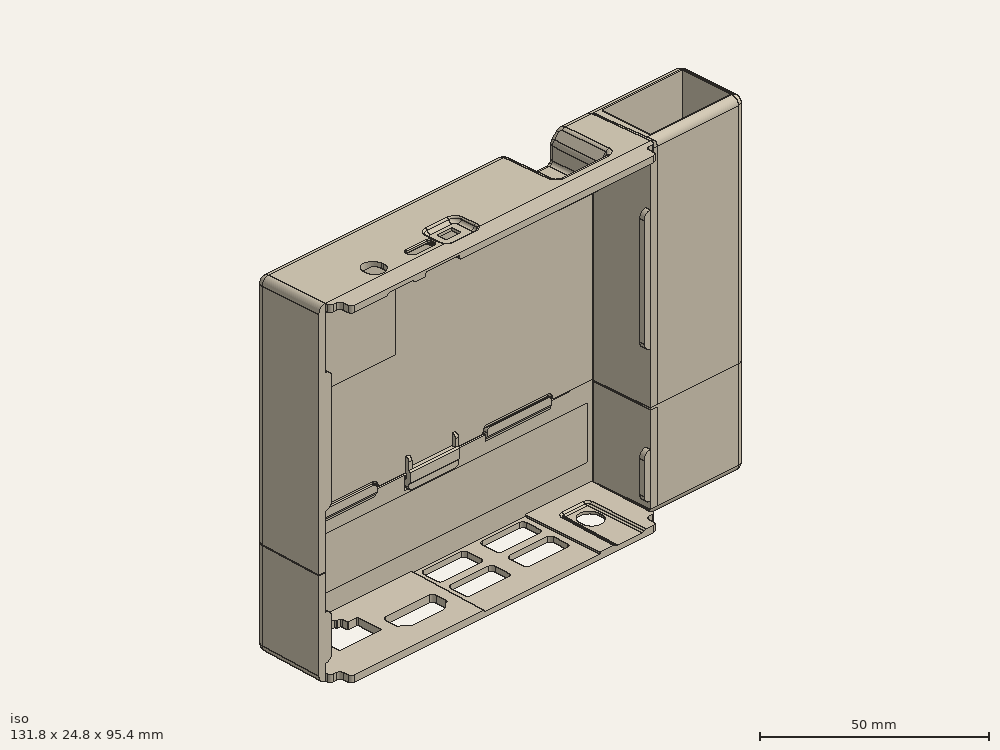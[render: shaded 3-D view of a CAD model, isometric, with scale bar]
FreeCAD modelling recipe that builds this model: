
FCSTD DOCUMENT  (FreeCAD 0.20R29177 +233 (Git))
Label: N2Case_10_11_2022
License: All rights reserved
LicenseURL: http://en.wikipedia.org/wiki/All_rights_reserved
objects: Part::Box×22, Part::Cylinder×11, Part::MultiFuse×9, Part::Cut×9, Part::Sphere×4, Part::Feature×2, Sketcher::SketchObject×2, PartDesign::Pad×2, PartDesign::Body×2
note: 65 computed .brp shape members not serialized (recipe doc carries the construction recipe); baked Part::Feature solids carry a one-line shape summary decoded from their .brp

FEATURE [Part::Feature] Solid  label="N2_BOTTOM_COVER"
  shape: bbox 104.6 x 25.21 x 71.78 mm, 343 faces (baked)
FEATURE [Part::Feature] Solid001  label="N2_TOP_COVER"
  shape: bbox 104.6 x 24.81 x 29.22 mm, 349 faces (baked)
FEATURE [Part::Box] Box  label="Cube"
  AttacherType = Attacher::AttachEngine3D
  Height = 15
  Length = 62.5
  Placement = pos=(-49,18,44) rot=(0,-1,0;4.71239rad)
  Width = 2
FEATURE [Part::MultiFuse] Fusion  label="BottomCover"
  Shapes = -> [Solid,Box]
FEATURE [Part::Box] Box001  label="Cube001"
  AttacherType = Attacher::AttachEngine3D
  Height = 15
  Length = 97.5
  Placement = pos=(48.5,20,-3.5) rot=(0,1,0;3.14159rad)
  Width = 2
FEATURE [Part::Cut] Cut
  Base = -> Fusion
  Tool = -> Box001
FEATURE [Part::Box] Box002  label="usbEthernet"
  AttacherType = Attacher::AttachEngine3D
  Height = 25
  Length = 72
  Placement = pos=(52.5,2.6,47.4) rot=(0,1,0;1.5708rad)
  Width = 15
FEATURE [Part::Box] Box003  label="usbEthernetCover"
  AttacherType = Attacher::AttachEngine3D
  Height = 27.5
  Length = 72
  Placement = pos=(50.5,2.2,47.4) rot=(0,1,0;1.5708rad)
  Width = 15.85
FEATURE [Part::Box] Box004  label="usbEthernetCover001"
  AttacherType = Attacher::AttachEngine3D
  Height = 27.52
  Length = 65.19
  Placement = pos=(49.98,17.6,45.39) rot=(0,1,0;1.5708rad)
  Width = 2.4
FEATURE [Part::Box] Box005  label="usbEthernetCover002"
  AttacherType = Attacher::AttachEngine3D
  Height = 2
  Length = 65.19
  Placement = pos=(77.5,2.2,45.39) rot=(0,1,0;1.5708rad)
  Width = 15.8
FEATURE [Part::Cylinder] Cylinder
  Angle = 90
  AttacherType = Attacher::AttachEngine3D
  FirstAngle = 0
  Height = 65.2
  Placement = pos=(77.5,2.2,-19.8) rot=(0,0,1;4.71239rad)
  Radius = 2
  SecondAngle = 0
FEATURE [Part::Cylinder] Cylinder001
  Angle = 90
  AttacherType = Attacher::AttachEngine3D
  FirstAngle = 0
  Height = 27.5
  Placement = pos=(77.5,18,45.4) rot=(0,1,0;4.71239rad)
  Radius = 2
  SecondAngle = 0
FEATURE [Part::Cylinder] Cylinder002
  Angle = 90
  AttacherType = Attacher::AttachEngine3D
  FirstAngle = 0
  Height = 15.8
  Placement = pos=(77.5,2.2,45.4) rot=(0.57735,0.57735,0.57735;4.18879rad)
  Radius = 2
  SecondAngle = 0
FEATURE [Part::Cylinder] Cylinder003
  Angle = 90
  AttacherType = Attacher::AttachEngine3D
  FirstAngle = 0
  Height = 65.2
  Placement = pos=(77.5,18,-19.8) rot=(0,0,1;0rad)
  Radius = 2
  SecondAngle = 0
FEATURE [Part::Box] Box006  label="usbEthernetCover003"
  AttacherType = Attacher::AttachEngine3D
  Height = 27.2
  Length = 65.19
  Placement = pos=(50.3,0.2,45.39) rot=(0,1,0;1.5708rad)
  Width = 2.4
FEATURE [Part::Cylinder] Cylinder004
  Angle = 90
  AttacherType = Attacher::AttachEngine3D
  FirstAngle = 0
  Height = 26.4
  Placement = pos=(77.5,2.2,45.4) rot=(-0.57735,0.57735,0.57735;4.18879rad)
  Radius = 2
  SecondAngle = 0
FEATURE [Part::Sphere] Sphere
  Angle1 = -90
  Angle2 = 90
  Angle3 = 360
  AttacherType = Attacher::AttachEngine3D
  Placement = pos=(77.5,18,45.4) rot=(0,0,1;0rad)
  Radius = 2
FEATURE [Part::Sphere] Sphere001
  Angle1 = -90
  Angle2 = 90
  Angle3 = 360
  AttacherType = Attacher::AttachEngine3D
  Placement = pos=(77.5,2.2,45.4) rot=(0,0,1;0rad)
  Radius = 2
FEATURE [Part::MultiFuse] Fusion001  label="usbCover"
  Shapes = -> [Box003,Box004,Box005,Cylinder,Cylinder001,Cylinder002,Cylinder003,Box006,Cylinder004,Sphere,Sphere001]
FEATURE [Part::MultiFuse] Fusion002
  Shapes = -> [Cut,Fusion001]
FEATURE [Part::Cut] Cut001  label="front"
  Base = -> Fusion002
  Tool = -> Box002
FEATURE [Part::Box] Box007  label="Cube002"
  AttacherType = Attacher::AttachEngine3D
  Height = 10
  Length = 30
  Placement = pos=(79.5,0,-19.8) rot=(0,1,0;3.14159rad)
  Width = 20
FEATURE [Part::Cut] Cut002
  Base = -> Cut001
  Tool = -> Box007
FEATURE [Part::Box] Box008  label="Cube003"
  AttacherType = Attacher::AttachEngine3D
  Height = 10
  Length = 30
  Placement = pos=(79.5,0,-19.8) rot=(0,1,0;3.14159rad)
  Width = 20
FEATURE [Part::Cut] Cut003  label="front001"
  Base = -> Cut002
  Tool = -> Box008
FEATURE [Part::Box] Box009  label="usbEthernet001"
  AttacherType = Attacher::AttachEngine3D
  Height = 25
  Length = 72
  Placement = pos=(52.5,2.6,6.3) rot=(0,1,0;1.5708rad)
  Width = 15
FEATURE [Part::Box] Box010  label="usbEthernetCover004"
  AttacherType = Attacher::AttachEngine3D
  Height = 27.5
  Length = 72
  Placement = pos=(50.5,2.2,-19.8) rot=(0,1,0;1.5708rad)
  Width = 15.85
FEATURE [Part::Box] Box011  label="usbEthernetCover005"
  AttacherType = Attacher::AttachEngine3D
  Height = 27.52
  Length = 65.19
  Placement = pos=(49.98,17.6,-19.8) rot=(0,1,0;1.5708rad)
  Width = 2.4
FEATURE [Part::Box] Box012  label="usbEthernetCover006"
  AttacherType = Attacher::AttachEngine3D
  Height = 2
  Length = 65.19
  Placement = pos=(77.5,2.2,-19.8) rot=(0,1,0;1.5708rad)
  Width = 15.8
FEATURE [Part::Box] Box013  label="usbEthernetCover007"
  AttacherType = Attacher::AttachEngine3D
  Height = 27.2
  Length = 65.19
  Placement = pos=(50.3,0.2,-19.8) rot=(0,1,0;1.5708rad)
  Width = 2.4
FEATURE [Part::Box] Box016  label="Cube005"
  AttacherType = Attacher::AttachEngine3D
  Height = 50
  Length = 29.5
  Placement = pos=(79.5,0,-45.4) rot=(0,1,0;3.14159rad)
  Width = 20
FEATURE [Part::MultiFuse] Fusion003
  Shapes = -> [Solid001,Box010,Box011,Box012,Box013]
FEATURE [Part::Cut] Cut004
  Base = -> Fusion003
  Tool = -> Box016
FEATURE [Part::Cut] Cut005
  Base = -> Cut004
  Tool = -> Box009
FEATURE [Part::Box] Box017  label="Cube006"
  AttacherType = Attacher::AttachEngine3D
  Height = 50
  Length = 23.5
  Placement = pos=(73.4,17.6,-45.39) rot=(0,1,0;3.14159rad)
  Width = 20
FEATURE [Part::Cut] Cut006
  Base = -> Cut005
  Tool = -> Box017
FEATURE [Part::Cylinder] Cylinder005
  Angle = 90
  AttacherType = Attacher::AttachEngine3D
  FirstAngle = 0
  Height = 65.2
  Placement = pos=(77.5,2.2,-45.4) rot=(0,0,-1;1.5708rad)
  Radius = 2
  SecondAngle = 0
FEATURE [Part::Cylinder] Cylinder006
  Angle = 90
  AttacherType = Attacher::AttachEngine3D
  FirstAngle = 0
  Height = 27.5
  Placement = pos=(77.5,18,-45.4) rot=(0,-1,0;1.5708rad)
  Radius = 2
  SecondAngle = 0
FEATURE [Part::Cylinder] Cylinder007
  Angle = 90
  AttacherType = Attacher::AttachEngine3D
  FirstAngle = 0
  Height = 15.8
  Placement = pos=(77.5,2.2,-45.4) rot=(-1,0,0;1.5708rad)
  Radius = 2
  SecondAngle = 0
FEATURE [Part::Cylinder] Cylinder008
  Angle = 90
  AttacherType = Attacher::AttachEngine3D
  FirstAngle = 0
  Height = 65.2
  Placement = pos=(77.5,18,-45.4) rot=(0,0,1;0rad)
  Radius = 2
  SecondAngle = 0
FEATURE [Part::Cylinder] Cylinder009
  Angle = 90
  AttacherType = Attacher::AttachEngine3D
  FirstAngle = 0
  Height = 27.6
  Placement = pos=(77.5,2.2,-45.4) rot=(-0.707107,0,0.707107;3.14159rad)
  Radius = 2
  SecondAngle = 0
FEATURE [Part::Cylinder] Cylinder010
  Angle = 90
  AttacherType = Attacher::AttachEngine3D
  FirstAngle = 0
  Height = 27.6
  Placement = pos=(77.5,18,-45.4) rot=(-0.57735,-0.57735,0.57735;2.0944rad)
  Radius = 2
  SecondAngle = 0
FEATURE [Part::Box] Box018  label="Cube007"
  AttacherType = Attacher::AttachEngine3D
  Height = 2
  Length = 27.6
  Placement = pos=(49.9,18,-45.4) rot=(1,0,0;3.14159rad)
  Width = 15.8
FEATURE [Part::Box] Box019  label="usbEthernet002"
  AttacherType = Attacher::AttachEngine3D
  Height = 25
  Length = 72
  Placement = pos=(52.5,2.6,-2.5) rot=(0,1,0;1.5708rad)
  Width = 15
FEATURE [Part::Sphere] Sphere002
  Angle1 = -90
  Angle2 = 90
  Angle3 = 360
  AttacherType = Attacher::AttachEngine3D
  Placement = pos=(77.5,18,-45.4) rot=(0,0,1;0rad)
  Radius = 2
FEATURE [Part::Sphere] Sphere003
  Angle1 = -90
  Angle2 = 90
  Angle3 = 360
  AttacherType = Attacher::AttachEngine3D
  Placement = pos=(77.5,2.2,-45.4) rot=(0,0,1;0rad)
  Radius = 2
FEATURE [Part::Box] Box020  label="Cube008"
  AttacherType = Attacher::AttachEngine3D
  Height = 40
  Length = 10
  Placement = pos=(73.6,0,-19.8) rot=(0,0,1;0rad)
  Width = 22
FEATURE [Part::MultiFuse] Fusion004  label="cuts"
  Shapes = -> [Box020,Box019]
FEATURE [Part::MultiFuse] Fusion005
  Shapes = -> [Sphere003,Cut006,Cylinder005,Cylinder006,Cylinder007,Cylinder008,Cylinder009,Cylinder010,Box018,Sphere002]
FEATURE [Part::Cut] Cut007  label="back"
  Base = -> Fusion005
  Tool = -> Fusion004
FEATURE [Part::Box] Box021  label="Cube009"
  AttacherType = Attacher::AttachEngine3D
  Height = 15
  Length = 97.5
  Placement = pos=(48.5,18,-25.1) rot=(0,1,0;3.14159rad)
  Width = 2
FEATURE [Part::MultiFuse] Fusion006  label="back001"
  Shapes = -> [Cut007,Box021]
FEATURE [Part::Box] Box068  label="logoBase001"
  AttacherType = Attacher::AttachEngine3D
  Height = 30
  Length = 35
  Placement = pos=(21.5,-44,15.25) rot=(0,0,1;0rad)
  Width = 1.8
FEATURE [Sketcher::SketchObject] Sketch001
  FullyConstrained = false
  MapMode = 5
  Support = -> [XY_Plane001]
  sketch-geometry (205):
    g0: LineSegment StartX=-15.0667 StartY=-2.9879 StartZ=0 EndX=-14.4175 EndY=-3.20194 EndZ=0
    g1: LineSegment StartX=-14.1386 StartY=-3.3581 StartZ=0 EndX=-13.8673 EndY=-3.55064 EndZ=0
    g2: LineSegment StartX=-10.8098 StartY=-4.00788 StartZ=0 EndX=-10.5716 EndY=-4.29909 EndZ=0
    g3: LineSegment StartX=-10.5716 StartY=-4.29909 StartZ=0 EndX=-10.1338 EndY=-4.33136 EndZ=0
    g4: LineSegment StartX=-10.1338 StartY=-4.33136 StartZ=0 EndX=-9.89036 EndY=-4.3898 EndZ=0
    g5: LineSegment StartX=-9.51656 StartY=-5.73022 StartZ=0 EndX=-9.24931 EndY=-5.76229 EndZ=0
    g6: LineSegment StartX=-9.24931 StartY=-5.76229 StartZ=0 EndX=-8.92861 EndY=-5.90126 EndZ=0
    g7: LineSegment StartX=-8.92861 StartY=-5.90126 StartZ=0 EndX=-8.54378 EndY=-5.86384 EndZ=0
    g8: LineSegment StartX=-8.54378 StartY=-5.86384 StartZ=0 EndX=-7.71788 EndY=-5.75845 EndZ=0
    g9: LineSegment StartX=-7.71788 StartY=-5.75845 StartZ=0 EndX=-7.37291 EndY=-5.97257 EndZ=0
    g10: LineSegment StartX=-7.37291 StartY=-5.97257 StartZ=0 EndX=-6.72487 EndY=-5.72038 EndZ=0
    g11: LineSegment StartX=-6.72487 StartY=-5.72038 StartZ=0 EndX=-6.27066 EndY=-5.69481 EndZ=0
    g12: LineSegment StartX=-6.27066 StartY=-5.69481 StartZ=0 EndX=-6.06223 EndY=-5.80493 EndZ=0
    g13: LineSegment StartX=-6.06223 StartY=-5.80493 StartZ=0 EndX=-5.35089 EndY=-5.48914 EndZ=0
    g14: LineSegment StartX=-5.35089 StartY=-5.48914 StartZ=0 EndX=-5.02402 EndY=-5.48914 EndZ=0
    g15: LineSegment StartX=-5.02402 StartY=-5.48914 StartZ=0 EndX=-4.80126 EndY=-5.53132 EndZ=0
    g16: LineSegment StartX=-4.80126 StartY=-5.53132 StartZ=0 EndX=-4.19735 EndY=-5.16248 EndZ=0
    g17: LineSegment StartX=-3.75191 StartY=-4.97251 StartZ=0 EndX=-3.37714 EndY=-4.97251 EndZ=0
    g18: LineSegment StartX=-3.37714 StartY=-4.97251 StartZ=0 EndX=-2.81898 EndY=-4.45422 EndZ=0
    g19: LineSegment StartX=-2.81898 StartY=-4.45422 StartZ=0 EndX=-2.62761 EndY=-4.34259 EndZ=0
    g20: LineSegment StartX=-2.62761 StartY=-4.34259 StartZ=0 EndX=-2.15112 EndY=-4.35765 EndZ=0
    g21: LineSegment StartX=-2.38042 StartY=-4.51801 StartZ=0 EndX=-3.18577 EndY=-5.42702 EndZ=0
    g22: LineSegment StartX=-3.18577 StartY=-5.42702 StartZ=0 EndX=-3.61318 EndY=-6.05824 EndZ=0
    g23: LineSegment StartX=-3.61318 StartY=-6.05824 StartZ=0 EndX=-3.7111 EndY=-6.64579 EndZ=0
    g24: LineSegment StartX=-3.7111 StartY=-6.64579 StartZ=0 EndX=-3.83514 EndY=-7.15501 EndZ=0
    g25: LineSegment StartX=-3.83514 StartY=-7.15501 StartZ=0 EndX=-3.75878 EndY=-7.50876 EndZ=0
    g26: LineSegment StartX=-3.75878 StartY=-7.50876 StartZ=0 EndX=-3.70596 EndY=-7.68135 EndZ=0
    g27: LineSegment StartX=-3.70596 StartY=-7.68135 StartZ=0 EndX=-3.53967 EndY=-7.85202 EndZ=0
    g28: LineSegment StartX=-3.53967 StartY=-7.85202 StartZ=0 EndX=-3.4685 EndY=-8.65617 EndZ=0
    g29: LineSegment StartX=-3.27268 StartY=-8.56671 StartZ=0 EndX=-3.16823 EndY=-8.76909 EndZ=0
    g30: LineSegment StartX=-3.07088 StartY=-9.32083 StartZ=0 EndX=-2.84207 EndY=-9.3355 EndZ=0
    g31: LineSegment StartX=-2.84207 StartY=-9.3355 StartZ=0 EndX=-2.45193 EndY=-10.0982 EndZ=0
    g32: LineSegment StartX=-2.45193 StartY=-10.0982 StartZ=0 EndX=-2.24953 EndY=-10.1304 EndZ=0
    g33: LineSegment StartX=-2.24953 StartY=-10.1304 StartZ=0 EndX=-0.96042 EndY=-11.8753 EndZ=0
    g34: LineSegment StartX=-0.96042 StartY=-11.8753 StartZ=0 EndX=-0.153326 EndY=-11.3889 EndZ=0
    g35: LineSegment StartX=-0.153326 StartY=-11.3889 StartZ=0 EndX=0.461347 EndY=-10.7689 EndZ=0
    g36: LineSegment StartX=0.461347 StartY=-10.7689 StartZ=0 EndX=0.669802 EndY=-10.7261 EndZ=0
    g37: LineSegment StartX=0.669802 StartY=-10.7261 StartZ=0 EndX=1.31724 EndY=-9.70998 EndZ=0
    g38: LineSegment StartX=1.31724 StartY=-9.70998 StartZ=0 EndX=1.51826 EndY=-9.65081 EndZ=0
    g39: LineSegment StartX=1.51826 StartY=-9.65081 StartZ=0 EndX=1.74022 EndY=-9.08937 EndZ=0
    g40: LineSegment StartX=1.74022 StartY=-9.08937 StartZ=0 EndX=2.02094 EndY=-9.04367 EndZ=0
    g41: LineSegment StartX=2.02094 StartY=-9.04367 StartZ=0 EndX=2.39306 EndY=-7.80327 EndZ=0
    g42: LineSegment StartX=2.39306 StartY=-7.80327 StartZ=0 EndX=2.58839 EndY=-7.69871 EndZ=0
    g43: LineSegment StartX=2.6542 StartY=-7.03945 StartZ=0 EndX=2.86963 EndY=-6.81749 EndZ=0
    g44: LineSegment StartX=2.86963 StartY=-6.81749 StartZ=0 EndX=3.0916 EndY=-6.92847 EndZ=0
    g45: LineSegment StartX=3.0916 StartY=-6.92847 StartZ=0 EndX=3.79666 EndY=-7.57478 EndZ=0
    g46: LineSegment StartX=3.79666 StartY=-7.57478 StartZ=0 EndX=3.93376 EndY=-7.50297 EndZ=0
    g47: LineSegment StartX=3.93376 StartY=-7.50297 StartZ=0 EndX=4.46256 EndY=-7.97301 EndZ=0
    g48: LineSegment StartX=4.46256 StartY=-7.97301 StartZ=0 EndX=4.68452 EndY=-7.92079 EndZ=0
    g49: LineSegment StartX=4.68452 StartY=-7.92079 StartZ=0 EndX=5.1154 EndY=-8.34513 EndZ=0
    g50: LineSegment StartX=5.1154 StartY=-8.34513 StartZ=0 EndX=5.32431 EndY=-8.28637 EndZ=0
    g51: LineSegment StartX=5.32431 StartY=-8.28637 StartZ=0 EndX=6.23668 EndY=-8.79564 EndZ=0
    g52: LineSegment StartX=6.23668 StartY=-8.79564 StartZ=0 EndX=6.50362 EndY=-8.76631 EndZ=0
    g53: LineSegment StartX=6.50362 StartY=-8.76631 StartZ=0 EndX=7.14802 EndY=-9.05537 EndZ=0
    g54: LineSegment StartX=7.14802 StartY=-9.05537 StartZ=0 EndX=8.04883 EndY=-9.18613 EndZ=0
    g55: LineSegment StartX=8.04883 StartY=-9.18613 StartZ=0 EndX=8.36847 EndY=-7.93662 EndZ=0
    g56: LineSegment StartX=8.36847 StartY=-7.93662 StartZ=0 EndX=8.49923 EndY=-7.79133 EndZ=0
    g57: LineSegment StartX=8.49923 StartY=-7.79133 StartZ=0 EndX=8.43477 EndY=-6.72206 EndZ=0
    g58: LineSegment StartX=8.43477 StartY=-6.72206 StartZ=0 EndX=8.58621 EndY=-6.47988 EndZ=0
    g59: LineSegment StartX=8.58621 StartY=-6.47988 StartZ=0 EndX=8.32296 EndY=-5.53178 EndZ=0
    g60: LineSegment StartX=8.32296 StartY=-5.53178 StartZ=0 EndX=8.43984 EndY=-5.19091 EndZ=0
    g61: LineSegment StartX=8.43984 StartY=-5.19091 StartZ=0 EndX=8.07426 EndY=-4.39307 EndZ=0
    g62: LineSegment StartX=8.07426 StartY=-4.39307 StartZ=0 EndX=8.04236 EndY=-4.17777 EndZ=0
    g63: LineSegment StartX=8.04236 StartY=-4.17777 StartZ=0 EndX=8.0902 EndY=-3.99438 EndZ=0
    g64: LineSegment StartX=8.4103 StartY=-4.11103 StartZ=0 EndX=8.72013 EndY=-4.0502 EndZ=0
    g65: LineSegment StartX=8.72013 StartY=-4.0502 StartZ=0 EndX=9.31817 EndY=-4.0502 EndZ=0
    g66: LineSegment StartX=9.31817 StartY=-4.0502 StartZ=0 EndX=9.82964 EndY=-4.15887 EndZ=0
    g67: LineSegment StartX=10.1326 StartY=-3.9675 StartZ=0 EndX=10.5175 EndY=-3.9623 EndZ=0
    g68: LineSegment StartX=10.5175 StartY=-3.9623 StartZ=0 EndX=10.8831 EndY=-3.97536 EndZ=0
    g69: LineSegment StartX=10.8831 StartY=-3.97536 StartZ=0 EndX=11.2245 EndY=-4.09431 EndZ=0
    g70: LineSegment StartX=11.2245 StartY=-4.09431 StartZ=0 EndX=11.6861 EndY=-3.91007 EndZ=0
    g71: LineSegment StartX=11.6861 StartY=-3.91007 StartZ=0 EndX=12.1039 EndY=-3.88396 EndZ=0
    g72: LineSegment StartX=12.1039 StartY=-3.88396 StartZ=0 EndX=12.6 EndY=-3.9623 EndZ=0
    g73: LineSegment StartX=12.6 StartY=-3.9623 StartZ=0 EndX=13.5793 EndY=-3.87743 EndZ=0
    g74: LineSegment StartX=13.5793 StartY=-3.87743 StartZ=0 EndX=14.3888 EndY=-3.74687 EndZ=0
    g75: LineSegment StartX=14.3888 StartY=-3.74687 StartZ=0 EndX=14.7544 EndY=-3.68158 EndZ=0
    g76: LineSegment StartX=14.7544 StartY=-3.68158 StartZ=0 EndX=15.2767 EndY=-3.75339 EndZ=0
    g77: LineSegment StartX=15.2767 StartY=-3.75339 StartZ=0 EndX=15.0432 EndY=-3.24137 EndZ=0
    g78: LineSegment StartX=15.0432 StartY=-3.24137 StartZ=0 EndX=14.5209 EndY=-2.51672 EndZ=0
    g79: LineSegment StartX=14.5209 StartY=-2.51672 StartZ=0 EndX=14.0378 EndY=-1.99445 EndZ=0
    g80: LineSegment StartX=14.0378 StartY=-1.99445 StartZ=0 EndX=13.2802 EndY=-1.54625 EndZ=0
    g81: LineSegment StartX=13.2802 StartY=-1.54625 StartZ=0 EndX=13.0438 EndY=-1.23117 EndZ=0
    g82: LineSegment StartX=13.0438 StartY=-1.23117 StartZ=0 EndX=12.1074 EndY=-0.797939 EndZ=0
    g83: LineSegment StartX=12.1074 StartY=-0.797939 StartZ=0 EndX=11.3804 EndY=-0.250878 EndZ=0
    g84: LineSegment StartX=11.3804 StartY=-0.250878 StartZ=0 EndX=10.4396 EndY=0.304889 EndZ=0
    g85: LineSegment StartX=10.4396 StartY=0.304889 StartZ=0 EndX=9.59526 EndY=0.727998 EndZ=0
    g86: LineSegment StartX=9.59526 StartY=0.727998 StartZ=0 EndX=8.53624 EndY=0.97306 EndZ=0
    g87: LineSegment StartX=8.53624 StartY=0.97306 StartZ=0 EndX=7.199 EndY=0.97306 EndZ=0
    g88: LineSegment StartX=7.199 StartY=0.97306 StartZ=0 EndX=5.77932 EndY=0.795578 EndZ=0
    g89: LineSegment StartX=5.77932 StartY=0.795578 StartZ=0 EndX=5.60186 EndY=0.795578 EndZ=0
    g90: LineSegment StartX=5.60186 StartY=0.795578 StartZ=0 EndX=5.83178 EndY=0.981815 EndZ=0
    g91: LineSegment StartX=5.83178 StartY=0.981815 StartZ=0 EndX=6.25403 EndY=1.1582 EndZ=0
    g92: LineSegment StartX=6.30214 StartY=1.38269 StartZ=0 EndX=7.17987 EndY=1.70686 EndZ=0
    g93: LineSegment StartX=7.17987 StartY=1.70686 StartZ=0 EndX=7.44682 EndY=1.79438 EndZ=0
    g94: LineSegment StartX=7.44682 StartY=1.79438 StartZ=0 EndX=7.49058 EndY=2.12696 EndZ=0
    g95: LineSegment StartX=7.49058 StartY=2.12696 StartZ=0 EndX=8.30058 EndY=2.66839 EndZ=0
    g96: LineSegment StartX=8.30058 StartY=2.66839 StartZ=0 EndX=8.68575 EndY=2.81854 EndZ=0
    g97: LineSegment StartX=8.68575 StartY=2.81854 StartZ=0 EndX=8.68575 EndY=3.12537 EndZ=0
    g98: LineSegment StartX=8.68575 StartY=3.12537 StartZ=0 EndX=8.89508 EndY=3.18684 EndZ=0
    g99: LineSegment StartX=8.89508 StartY=3.18684 StartZ=0 EndX=9.63492 EndY=4.06602 EndZ=0
    g100: LineSegment StartX=9.63492 StartY=4.06602 StartZ=0 EndX=9.62638 EndY=4.32743 EndZ=0
    g101: LineSegment StartX=9.62638 StartY=4.32743 StartZ=0 EndX=10.2068 EndY=5.18314 EndZ=0
    g102: LineSegment StartX=10.2068 StartY=5.18314 StartZ=0 EndX=9.25518 EndY=5.64445 EndZ=0
    g103: LineSegment StartX=9.1102 StartY=5.87597 StartZ=0 EndX=8.32132 EndY=5.97336 EndZ=0
    g104: LineSegment StartX=8.32132 StartY=5.97336 StartZ=0 EndX=8.15466 EndY=6.06625 EndZ=0
    g105: LineSegment StartX=7.63471 StartY=6.13088 StartZ=0 EndX=7.56391 EndY=6.33267 EndZ=0
    g106: LineSegment StartX=7.56391 StartY=6.33267 StartZ=0 EndX=6.74832 EndY=6.35496 EndZ=0
    g107: LineSegment StartX=6.74832 StartY=6.35496 StartZ=0 EndX=6.46819 EndY=6.29526 EndZ=0
    g108: LineSegment StartX=6.46819 StartY=6.29526 StartZ=0 EndX=6.27042 EndY=6.61061 EndZ=0
    g109: LineSegment StartX=6.27042 StartY=6.61061 StartZ=0 EndX=5.40453 EndY=6.33267 EndZ=0
    g110: LineSegment StartX=5.40453 StartY=6.33267 StartZ=0 EndX=5.27091 EndY=6.47164 EndZ=0
    g111: LineSegment StartX=5.27091 StartY=6.47164 StartZ=0 EndX=4.56942 EndY=6.24725 EndZ=0
    g112: LineSegment StartX=4.56942 StartY=6.24725 StartZ=0 EndX=4.44161 EndY=6.40652 EndZ=0
    g113: LineSegment StartX=4.44161 StartY=6.40652 StartZ=0 EndX=3.4195 EndY=5.94588 EndZ=0
    g114: LineSegment StartX=3.4195 StartY=5.94588 StartZ=0 EndX=3.29192 EndY=6.1532 EndZ=0
    g115: LineSegment StartX=3.29192 StartY=6.1532 StartZ=0 EndX=2.15964 EndY=5.49137 EndZ=0
    g116: LineSegment StartX=2.15964 StartY=5.49137 StartZ=0 EndX=2.00016 EndY=5.69869 EndZ=0
    g117: LineSegment StartX=2.00016 StartY=5.69869 StartZ=0 EndX=1.6185 EndY=5.34828 EndZ=0
    g118: LineSegment StartX=1.6185 StartY=5.34828 StartZ=0 EndX=1.45984 EndY=5.94974 EndZ=0
    g119: LineSegment StartX=1.38165 StartY=6.28651 StartZ=0 EndX=1.14534 EndY=6.29963 EndZ=0
    g120: LineSegment StartX=0.348522 StartY=7.29544 StartZ=0 EndX=0.126706 EndY=7.68126 EndZ=0
    g121: LineSegment StartX=0.126706 StartY=7.68126 StartZ=0 EndX=-0.415308 EndY=8.18163 EndZ=0
    g122: LineSegment StartX=-0.415308 StartY=8.18163 StartZ=0 EndX=-0.872658 EndY=8.6237 EndZ=0
    g123: LineSegment StartX=-0.872658 StartY=8.6237 StartZ=0 EndX=-1.12074 EndY=8.64329 EndZ=0
    g124: LineSegment StartX=-1.12074 StartY=8.64329 StartZ=0 EndX=-1.79316 EndY=9.11986 EndZ=0
    g125: LineSegment StartX=-1.79316 StartY=9.11986 StartZ=0 EndX=-2.31488 EndY=9.12122 EndZ=0
    g126: LineSegment StartX=-2.31488 StartY=9.12122 StartZ=0 EndX=-2.71321 EndY=9.13846 EndZ=0
    g127: LineSegment StartX=-2.71321 StartY=9.13846 StartZ=0 EndX=-2.88425 EndY=9.34157 EndZ=0
    g128: LineSegment StartX=-2.88425 StartY=9.34157 StartZ=0 EndX=-3.16779 EndY=9.26454 EndZ=0
    g129: LineSegment StartX=-3.70739 StartY=9.82796 StartZ=0 EndX=-4.04915 EndY=9.7003 EndZ=0
    g130: LineSegment StartX=-4.04915 StartY=9.7003 StartZ=0 EndX=-4.42988 EndY=10.011 EndZ=0
    g131: LineSegment StartX=-5.98947 StartY=10.3656 StartZ=0 EndX=-7.32605 EndY=10.4108 EndZ=0
    g132: LineSegment StartX=-7.25254 StartY=9.13254 StartZ=0 EndX=-7.36878 EndY=8.7693 EndZ=0
    g133: LineSegment StartX=-7.36878 StartY=8.7693 StartZ=0 EndX=-7.2614 EndY=7.83762 EndZ=0
    g134: LineSegment StartX=-7.2614 StartY=7.83762 StartZ=0 EndX=-7.41112 EndY=7.6042 EndZ=0
    g135: LineSegment StartX=-7.41112 StartY=7.6042 StartZ=0 EndX=-7.09216 EndY=6.74302 EndZ=0
    g136: LineSegment StartX=-7.09216 StartY=6.74302 StartZ=0 EndX=-7.10014 EndY=6.55962 EndZ=0
    g137: LineSegment StartX=-7.10014 StartY=6.55962 StartZ=0 EndX=-7.29151 EndY=6.3842 EndZ=0
    g138: LineSegment StartX=-7.29151 StartY=6.3842 StartZ=0 EndX=-6.74132 EndY=5.29976 EndZ=0
    g139: LineSegment StartX=-6.74132 StartY=5.29976 StartZ=0 EndX=-6.87495 EndY=5.02732 EndZ=0
    g140: LineSegment StartX=-6.87495 StartY=5.02732 StartZ=0 EndX=-6.31586 EndY=4.42065 EndZ=0
    g141: LineSegment StartX=-6.31586 StartY=4.42065 StartZ=0 EndX=-6.30396 EndY=4.19463 EndZ=0
    g142: LineSegment StartX=-6.30396 StartY=4.19463 StartZ=0 EndX=-6.05415 EndY=4.0043 EndZ=0
    g143: LineSegment StartX=-6.05415 StartY=4.0043 StartZ=0 EndX=-6.18501 EndY=3.95672 EndZ=0
    g144: LineSegment StartX=-6.18501 StartY=3.95672 StartZ=0 EndX=-5.54265 EndY=3.07645 EndZ=0
    g145: LineSegment StartX=-5.54265 StartY=3.07645 StartZ=0 EndX=-5.57833 EndY=2.90991 EndZ=0
    g146: LineSegment StartX=-5.57833 StartY=2.90991 StartZ=0 EndX=-5.1263 EndY=2.41029 EndZ=0
    g147: LineSegment StartX=-5.1263 StartY=2.41029 StartZ=0 EndX=-5.18578 EndY=2.26755 EndZ=0
    g148: LineSegment StartX=-5.18578 StartY=2.26755 StartZ=0 EndX=-4.73375 EndY=1.89878 EndZ=0
    g149: LineSegment StartX=-4.73375 StartY=1.89878 StartZ=0 EndX=-4.42446 EndY=1.5895 EndZ=0
    g150: LineSegment StartX=-4.42446 StartY=1.5895 StartZ=0 EndX=-5.31663 EndY=1.29211 EndZ=0
    g151: LineSegment StartX=-5.31663 StartY=1.29211 StartZ=0 EndX=-5.84004 EndY=1.08988 EndZ=0
    g152: LineSegment StartX=-5.84004 StartY=1.08988 StartZ=0 EndX=-6.04226 EndY=0.792495 EndZ=0
    g153: LineSegment StartX=-6.04226 StartY=0.792495 StartZ=0 EndX=-6.94632 EndY=0.994719 EndZ=0
    g154: LineSegment StartX=-6.94632 StartY=0.994719 StartZ=0 EndX=-7.19613 EndY=0.887659 EndZ=0
    g155: LineSegment StartX=-7.19613 StartY=0.887659 StartZ=0 EndX=-7.8147 EndY=1.0423 EndZ=0
    g156: LineSegment StartX=-7.8147 StartY=1.0423 StartZ=0 EndX=-8.02502 EndY=0.969153 EndZ=0
    g157: LineSegment StartX=-8.02502 StartY=0.969153 StartZ=0 EndX=-8.60267 EndY=1.03042 EndZ=0
    g158: LineSegment StartX=-8.60267 StartY=1.03042 StartZ=0 EndX=-8.8346 EndY=0.872878 EndZ=0
    g159: LineSegment StartX=-8.8346 StartY=0.872878 StartZ=0 EndX=-9.33349 EndY=0.929767 EndZ=0
    g160: LineSegment StartX=-9.33349 StartY=0.929767 StartZ=0 EndX=-9.66169 EndY=0.649695 EndZ=0
    g161: LineSegment StartX=-9.66169 StartY=0.649695 StartZ=0 EndX=-10.3249 EndY=0.649695 EndZ=0
    g162: LineSegment StartX=-10.3249 StartY=0.649695 StartZ=0 EndX=-11.0107 EndY=0.32425 EndZ=0
    g163: LineSegment StartX=-11.0107 StartY=0.32425 StartZ=0 EndX=-11.7283 EndY=0.053139 EndZ=0
    g164: LineSegment StartX=-11.7283 StartY=0.053139 StartZ=0 EndX=-12.2971 EndY=-0.13161 EndZ=0
    g165: LineSegment StartX=-12.2971 StartY=-0.13161 StartZ=0 EndX=-12.4212 EndY=-0.347049 EndZ=0
    g166: LineSegment StartX=-12.4212 StartY=-0.347049 StartZ=0 EndX=-13.296 EndY=-0.817096 EndZ=0
    g167: LineSegment StartX=-13.296 StartY=-0.817096 StartZ=0 EndX=-13.9227 EndY=-1.24144 EndZ=0
    g168: LineSegment StartX=-13.9227 StartY=-1.24144 StartZ=0 EndX=-14.1708 EndY=-1.59398 EndZ=0
    g169: LineSegment StartX=-14.1708 StartY=-1.59398 StartZ=0 EndX=-14.5386 EndY=-2.09216 EndZ=0
    g170: LineSegment StartX=-14.5386 StartY=-2.09216 StartZ=0 EndX=-14.7831 EndY=-2.4577 EndZ=0
    g171: LineSegment StartX=-14.7831 StartY=-2.4577 StartZ=0 EndX=-15.0667 EndY=-2.9879 EndZ=0
    g172: LineSegment StartX=7.82861 StartY=6.04487 StartZ=0 EndX=7.63471 EndY=6.13088 EndZ=0
    g173: LineSegment StartX=-14.4175 StartY=-3.20194 StartZ=0 EndX=-14.1386 EndY=-3.3581 EndZ=0
    g174: LineSegment StartX=-13.8673 StartY=-3.55064 StartZ=0 EndX=-13.4107 EndY=-3.57136 EndZ=0
    g175: LineSegment StartX=-13.1321 StartY=-3.61699 StartZ=0 EndX=-12.817 EndY=-3.62343 EndZ=0
    g176: LineSegment StartX=-12.817 StartY=-3.62343 StartZ=0 EndX=-12.4662 EndY=-3.85302 EndZ=0
    g177: LineSegment StartX=-13.4107 StartY=-3.57136 StartZ=0 EndX=-13.1321 EndY=-3.61699 EndZ=0
    g178: LineSegment StartX=-12.4662 StartY=-3.85302 StartZ=0 EndX=-11.8704 EndY=-3.85302 EndZ=0
    g179: LineSegment StartX=-11.8704 StartY=-3.85302 StartZ=0 EndX=-11.5204 EndY=-4.00836 EndZ=0
    g180: LineSegment StartX=-11.5204 StartY=-4.00836 StartZ=0 EndX=-11.1389 EndY=-4.05555 EndZ=0
    g181: LineSegment StartX=-11.1389 StartY=-4.05555 StartZ=0 EndX=-10.8098 EndY=-4.00788 EndZ=0
    g182: LineSegment StartX=-9.89036 StartY=-4.3898 StartZ=0 EndX=-9.99555 EndY=-4.87697 EndZ=0
    g183: LineSegment StartX=-9.99555 StartY=-4.87697 StartZ=0 EndX=-10.0894 EndY=-5.36391 EndZ=0
    g184: LineSegment StartX=-10.0894 StartY=-5.36391 StartZ=0 EndX=-10.107 EndY=-5.50471 EndZ=0
    g185: LineSegment StartX=-10.107 StartY=-5.50471 StartZ=0 EndX=-9.77848 EndY=-5.63965 EndZ=0
    g186: LineSegment StartX=-9.77848 StartY=-5.63965 StartZ=0 EndX=-9.51656 EndY=-5.73022 EndZ=0
    g187: LineSegment StartX=-4.19735 StartY=-5.16248 StartZ=0 EndX=-3.75191 EndY=-4.97251 EndZ=0
    g188: LineSegment StartX=-2.38042 StartY=-4.51801 StartZ=0 EndX=-2.15112 EndY=-4.35765 EndZ=0
    g189: LineSegment StartX=-3.4685 StartY=-8.65617 StartZ=0 EndX=-3.27268 EndY=-8.56671 EndZ=0
    g190: LineSegment StartX=-3.16823 StartY=-8.76909 StartZ=0 EndX=-3.07088 EndY=-9.32083 EndZ=0
    g191: LineSegment StartX=2.58839 StartY=-7.69871 StartZ=0 EndX=2.6542 EndY=-7.03945 EndZ=0
    g192: LineSegment StartX=8.0902 StartY=-3.99438 StartZ=0 EndX=8.4103 EndY=-4.11103 EndZ=0
    g193: LineSegment StartX=9.82964 StartY=-4.15887 StartZ=0 EndX=10.1326 EndY=-3.9675 EndZ=0
    g194: LineSegment StartX=6.30214 StartY=1.38269 StartZ=0 EndX=6.25403 EndY=1.1582 EndZ=0
    g195: LineSegment StartX=1.38165 StartY=6.28651 StartZ=0 EndX=1.45984 EndY=5.94974 EndZ=0
    g196: LineSegment StartX=0.348522 StartY=7.29544 StartZ=0 EndX=0.824344 EndY=6.91479 EndZ=0
    g197: LineSegment StartX=0.824344 StartY=6.91479 StartZ=0 EndX=1.14534 EndY=6.29963 EndZ=0
    g198: LineSegment StartX=-3.70739 StartY=9.82796 StartZ=0 EndX=-3.16779 EndY=9.26454 EndZ=0
    g199: LineSegment StartX=-5.98947 StartY=10.3656 StartZ=0 EndX=-5.43038 EndY=10.4489 EndZ=0
    g200: LineSegment StartX=-5.43038 StartY=10.4489 StartZ=0 EndX=-4.9791 EndY=10.1425 EndZ=0
    g201: LineSegment StartX=-4.42988 StartY=10.011 StartZ=0 EndX=-4.9791 EndY=10.1425 EndZ=0
    g202: LineSegment StartX=-7.25254 StartY=9.13254 StartZ=0 EndX=-7.32605 EndY=10.4108 EndZ=0
    g203: LineSegment StartX=7.82861 StartY=6.04487 StartZ=0 EndX=8.15466 EndY=6.06625 EndZ=0
    g204: LineSegment StartX=9.1102 StartY=5.87597 StartZ=0 EndX=9.25518 EndY=5.64445 EndZ=0
  constraints (114):
    c: Coincident(g4,g3)
    c: Coincident(g6,g5)
    c: Coincident(g8,g7)
    c: Coincident(g9,g8)
    c: Coincident(g10,g9)
    c: Coincident(g11,g10)
    c: Coincident(g13,g12)
    c: Coincident(g16,g15)
    c: Coincident(g22,g21)
    c: Coincident(g25,g24)
    c: Coincident(g26,g25)
    c: Coincident(g28,g27)
    c: Coincident(g33,g32)
    c: Coincident(g37,g36)
    c: Coincident(g38,g37)
    c: Coincident(g40,g39)
    c: Coincident(g44,g43)
    c: Coincident(g51,g50)
    c: Coincident(g52,g51)
    c: Coincident(g57,g56)
    c: Coincident(g58,g57)
    c: Coincident(g59,g58)
    c: Coincident(g61,g60)
    c: Coincident(g63,g62)
    c: Coincident(g66,g65)
    c: Coincident(g70,g69)
    c: Coincident(g72,g71)
    c: Coincident(g73,g72)
    c: Coincident(g74,g73)
    c: Coincident(g77,g76)
    c: Coincident(g80,g79)
    c: Coincident(g81,g80)
    c: Coincident(g83,g82)
    c: Coincident(g85,g84)
    c: Coincident(g86,g85)
    c: Coincident(g87,g86)
    c: Coincident(g89,g88)
    c: Coincident(g90,g89)
    c: Coincident(g91,g90)
    c: Coincident(g93,g92)
    c: Coincident(g95,g94)
    c: Coincident(g97,g96)
    c: Coincident(g98,g97)
    c: Coincident(g99,g98)
    c: Coincident(g100,g99)
    c: Coincident(g104,g103)
    c: Coincident(g106,g105)
    c: Coincident(g107,g106)
    c: Coincident(g111,g110)
    c: Coincident(g113,g112)
    c: Coincident(g118,g117)
    c: Coincident(g122,g121)
    c: Coincident(g126,g125)
    c: Coincident(g130,g129)
    c: Coincident(g133,g132)
    c: Coincident(g134,g133)
    c: Coincident(g135,g134)
    c: Coincident(g139,g138)
    c: Coincident(g142,g141)
    c: Coincident(g156,g155)
    c: Coincident(g157,g156)
    c: Coincident(g159,g158)
    c: Coincident(g161,g160)
    c: Coincident(g164,g163)
    c: Coincident(g165,g164)
    c: Coincident(g168,g167)
    c: Coincident(g169,g168)
    c: Coincident(g171,g170)
    c: Coincident(g171,g0)
    c: Coincident(g172,g105)
    c: DistanceX(g165) = -12.4212
    c: DistanceY(g165) = -0.347049
    c: Coincident(g173,g0)
    c: Coincident(g173,g1)
    c: Coincident(g174,g1)
    c: Coincident(g177,g174)
    c: Coincident(g177,g175)
    c: Coincident(g178,g176)
    c: Coincident(g181,g2)
    c: Coincident(g182,g4)
    c: Coincident(g186,g185)
    c: Coincident(g186,g5)
    c: Coincident(g187,g16)
    c: Coincident(g187,g17)
    c: Coincident(g188,g21)
    c: Coincident(g188,g20)
    c: Coincident(g189,g28)
    c: Coincident(g189,g29)
    c: Coincident(g190,g29)
    c: Coincident(g190,g30)
    c: Coincident(g191,g42)
    c: Coincident(g191,g43)
    c: Coincident(g192,g63)
    c: Coincident(g192,g64)
    c: Coincident(g193,g66)
    c: Coincident(g193,g67)
    c: Coincident(g194,g92)
    c: Coincident(g194,g91)
    c: Coincident(g195,g119)
    c: Coincident(g195,g118)
    c: Coincident(g196,g120)
    c: Coincident(g197,g119)
    c: Coincident(g198,g129)
    c: Coincident(g198,g128)
    c: Coincident(g199,g131)
    c: Coincident(g200,g199)
    c: Coincident(g201,g130)
    c: Coincident(g201,g200)
    c: Coincident(g202,g132)
    c: Coincident(g202,g131)
    c: Coincident(g203,g172)
    c: Coincident(g203,g104)
    c: Coincident(g204,g103)
    c: Coincident(g204,g102)
FEATURE [PartDesign::Pad] Pad001
  Direction = (0,0,1)
  Length = 3
  Length2 = 10
  Profile = -> Sketch001
  ReferenceAxis = -> Sketch001 [N_Axis]
  Type = 0
FEATURE [PartDesign::Body] Body001  label="logo002"
  Group = -> [Sketch001,Pad001]
  Origin = -> Origin001
  Placement = pos=(39.35,-43,30) rot=(1,0,0;1.5708rad)
  Tip = -> Pad001
FEATURE [Part::MultiFuse] Fusion040  label="logo003"
  Placement = pos=(-69,-26,58) rot=(1,0,0;3.14159rad)
  Shapes = -> [Body001,Box068]
FEATURE [Part::Cut] Cut008  label="front002"
  Base = -> Cut003
  Tool = -> Fusion040
FEATURE [Part::Box] Box069  label="logoBase002"
  AttacherType = Attacher::AttachEngine3D
  Height = 30
  Length = 35
  Placement = pos=(21.5,-44,15.25) rot=(0,0,1;0rad)
  Width = 1.8
FEATURE [Sketcher::SketchObject] Sketch002
  FullyConstrained = false
  MapMode = 5
  Support = -> [XY_Plane002]
  sketch-geometry (205):
    g0: LineSegment StartX=-15.0667 StartY=-2.9879 StartZ=0 EndX=-14.4175 EndY=-3.20194 EndZ=0
    g1: LineSegment StartX=-14.1386 StartY=-3.3581 StartZ=0 EndX=-13.8673 EndY=-3.55064 EndZ=0
    g2: LineSegment StartX=-10.8098 StartY=-4.00788 StartZ=0 EndX=-10.5716 EndY=-4.29909 EndZ=0
    g3: LineSegment StartX=-10.5716 StartY=-4.29909 StartZ=0 EndX=-10.1338 EndY=-4.33136 EndZ=0
    g4: LineSegment StartX=-10.1338 StartY=-4.33136 StartZ=0 EndX=-9.89036 EndY=-4.3898 EndZ=0
    g5: LineSegment StartX=-9.51656 StartY=-5.73022 StartZ=0 EndX=-9.24931 EndY=-5.76229 EndZ=0
    g6: LineSegment StartX=-9.24931 StartY=-5.76229 StartZ=0 EndX=-8.92861 EndY=-5.90126 EndZ=0
    g7: LineSegment StartX=-8.92861 StartY=-5.90126 StartZ=0 EndX=-8.54378 EndY=-5.86384 EndZ=0
    g8: LineSegment StartX=-8.54378 StartY=-5.86384 StartZ=0 EndX=-7.71788 EndY=-5.75845 EndZ=0
    g9: LineSegment StartX=-7.71788 StartY=-5.75845 StartZ=0 EndX=-7.37291 EndY=-5.97257 EndZ=0
    g10: LineSegment StartX=-7.37291 StartY=-5.97257 StartZ=0 EndX=-6.72487 EndY=-5.72038 EndZ=0
    g11: LineSegment StartX=-6.72487 StartY=-5.72038 StartZ=0 EndX=-6.27066 EndY=-5.69481 EndZ=0
    g12: LineSegment StartX=-6.27066 StartY=-5.69481 StartZ=0 EndX=-6.06223 EndY=-5.80493 EndZ=0
    g13: LineSegment StartX=-6.06223 StartY=-5.80493 StartZ=0 EndX=-5.35089 EndY=-5.48914 EndZ=0
    g14: LineSegment StartX=-5.35089 StartY=-5.48914 StartZ=0 EndX=-5.02402 EndY=-5.48914 EndZ=0
    g15: LineSegment StartX=-5.02402 StartY=-5.48914 StartZ=0 EndX=-4.80126 EndY=-5.53132 EndZ=0
    g16: LineSegment StartX=-4.80126 StartY=-5.53132 StartZ=0 EndX=-4.19735 EndY=-5.16248 EndZ=0
    g17: LineSegment StartX=-3.75191 StartY=-4.97251 StartZ=0 EndX=-3.37714 EndY=-4.97251 EndZ=0
    g18: LineSegment StartX=-3.37714 StartY=-4.97251 StartZ=0 EndX=-2.81898 EndY=-4.45422 EndZ=0
    g19: LineSegment StartX=-2.81898 StartY=-4.45422 StartZ=0 EndX=-2.62761 EndY=-4.34259 EndZ=0
    g20: LineSegment StartX=-2.62761 StartY=-4.34259 StartZ=0 EndX=-2.15112 EndY=-4.35765 EndZ=0
    g21: LineSegment StartX=-2.38042 StartY=-4.51801 StartZ=0 EndX=-3.18577 EndY=-5.42702 EndZ=0
    g22: LineSegment StartX=-3.18577 StartY=-5.42702 StartZ=0 EndX=-3.61318 EndY=-6.05824 EndZ=0
    g23: LineSegment StartX=-3.61318 StartY=-6.05824 StartZ=0 EndX=-3.7111 EndY=-6.64579 EndZ=0
    g24: LineSegment StartX=-3.7111 StartY=-6.64579 StartZ=0 EndX=-3.83514 EndY=-7.15501 EndZ=0
    g25: LineSegment StartX=-3.83514 StartY=-7.15501 StartZ=0 EndX=-3.75878 EndY=-7.50876 EndZ=0
    g26: LineSegment StartX=-3.75878 StartY=-7.50876 StartZ=0 EndX=-3.70596 EndY=-7.68135 EndZ=0
    g27: LineSegment StartX=-3.70596 StartY=-7.68135 StartZ=0 EndX=-3.53967 EndY=-7.85202 EndZ=0
    g28: LineSegment StartX=-3.53967 StartY=-7.85202 StartZ=0 EndX=-3.4685 EndY=-8.65617 EndZ=0
    g29: LineSegment StartX=-3.27268 StartY=-8.56671 StartZ=0 EndX=-3.16823 EndY=-8.76909 EndZ=0
    g30: LineSegment StartX=-3.07088 StartY=-9.32083 StartZ=0 EndX=-2.84207 EndY=-9.3355 EndZ=0
    g31: LineSegment StartX=-2.84207 StartY=-9.3355 StartZ=0 EndX=-2.45193 EndY=-10.0982 EndZ=0
    g32: LineSegment StartX=-2.45193 StartY=-10.0982 StartZ=0 EndX=-2.24953 EndY=-10.1304 EndZ=0
    g33: LineSegment StartX=-2.24953 StartY=-10.1304 StartZ=0 EndX=-0.96042 EndY=-11.8753 EndZ=0
    g34: LineSegment StartX=-0.96042 StartY=-11.8753 StartZ=0 EndX=-0.153326 EndY=-11.3889 EndZ=0
    g35: LineSegment StartX=-0.153326 StartY=-11.3889 StartZ=0 EndX=0.461347 EndY=-10.7689 EndZ=0
    g36: LineSegment StartX=0.461347 StartY=-10.7689 StartZ=0 EndX=0.669802 EndY=-10.7261 EndZ=0
    g37: LineSegment StartX=0.669802 StartY=-10.7261 StartZ=0 EndX=1.31724 EndY=-9.70998 EndZ=0
    g38: LineSegment StartX=1.31724 StartY=-9.70998 StartZ=0 EndX=1.51826 EndY=-9.65081 EndZ=0
    g39: LineSegment StartX=1.51826 StartY=-9.65081 StartZ=0 EndX=1.74022 EndY=-9.08937 EndZ=0
    g40: LineSegment StartX=1.74022 StartY=-9.08937 StartZ=0 EndX=2.02094 EndY=-9.04367 EndZ=0
    g41: LineSegment StartX=2.02094 StartY=-9.04367 StartZ=0 EndX=2.39306 EndY=-7.80327 EndZ=0
    g42: LineSegment StartX=2.39306 StartY=-7.80327 StartZ=0 EndX=2.58839 EndY=-7.69871 EndZ=0
    g43: LineSegment StartX=2.6542 StartY=-7.03945 StartZ=0 EndX=2.86963 EndY=-6.81749 EndZ=0
    g44: LineSegment StartX=2.86963 StartY=-6.81749 StartZ=0 EndX=3.0916 EndY=-6.92847 EndZ=0
    g45: LineSegment StartX=3.0916 StartY=-6.92847 StartZ=0 EndX=3.79666 EndY=-7.57478 EndZ=0
    g46: LineSegment StartX=3.79666 StartY=-7.57478 StartZ=0 EndX=3.93376 EndY=-7.50297 EndZ=0
    g47: LineSegment StartX=3.93376 StartY=-7.50297 StartZ=0 EndX=4.46256 EndY=-7.97301 EndZ=0
    g48: LineSegment StartX=4.46256 StartY=-7.97301 StartZ=0 EndX=4.68452 EndY=-7.92079 EndZ=0
    g49: LineSegment StartX=4.68452 StartY=-7.92079 StartZ=0 EndX=5.1154 EndY=-8.34513 EndZ=0
    g50: LineSegment StartX=5.1154 StartY=-8.34513 StartZ=0 EndX=5.32431 EndY=-8.28637 EndZ=0
    g51: LineSegment StartX=5.32431 StartY=-8.28637 StartZ=0 EndX=6.23668 EndY=-8.79564 EndZ=0
    g52: LineSegment StartX=6.23668 StartY=-8.79564 StartZ=0 EndX=6.50362 EndY=-8.76631 EndZ=0
    g53: LineSegment StartX=6.50362 StartY=-8.76631 StartZ=0 EndX=7.14802 EndY=-9.05537 EndZ=0
    g54: LineSegment StartX=7.14802 StartY=-9.05537 StartZ=0 EndX=8.04883 EndY=-9.18613 EndZ=0
    g55: LineSegment StartX=8.04883 StartY=-9.18613 StartZ=0 EndX=8.36847 EndY=-7.93662 EndZ=0
    g56: LineSegment StartX=8.36847 StartY=-7.93662 StartZ=0 EndX=8.49923 EndY=-7.79133 EndZ=0
    g57: LineSegment StartX=8.49923 StartY=-7.79133 StartZ=0 EndX=8.43477 EndY=-6.72206 EndZ=0
    g58: LineSegment StartX=8.43477 StartY=-6.72206 StartZ=0 EndX=8.58621 EndY=-6.47988 EndZ=0
    g59: LineSegment StartX=8.58621 StartY=-6.47988 StartZ=0 EndX=8.32296 EndY=-5.53178 EndZ=0
    g60: LineSegment StartX=8.32296 StartY=-5.53178 StartZ=0 EndX=8.43984 EndY=-5.19091 EndZ=0
    g61: LineSegment StartX=8.43984 StartY=-5.19091 StartZ=0 EndX=8.07426 EndY=-4.39307 EndZ=0
    g62: LineSegment StartX=8.07426 StartY=-4.39307 StartZ=0 EndX=8.04236 EndY=-4.17777 EndZ=0
    g63: LineSegment StartX=8.04236 StartY=-4.17777 StartZ=0 EndX=8.0902 EndY=-3.99438 EndZ=0
    g64: LineSegment StartX=8.4103 StartY=-4.11103 StartZ=0 EndX=8.72013 EndY=-4.0502 EndZ=0
    g65: LineSegment StartX=8.72013 StartY=-4.0502 StartZ=0 EndX=9.31817 EndY=-4.0502 EndZ=0
    g66: LineSegment StartX=9.31817 StartY=-4.0502 StartZ=0 EndX=9.82964 EndY=-4.15887 EndZ=0
    g67: LineSegment StartX=10.1326 StartY=-3.9675 StartZ=0 EndX=10.5175 EndY=-3.9623 EndZ=0
    g68: LineSegment StartX=10.5175 StartY=-3.9623 StartZ=0 EndX=10.8831 EndY=-3.97536 EndZ=0
    g69: LineSegment StartX=10.8831 StartY=-3.97536 StartZ=0 EndX=11.2245 EndY=-4.09431 EndZ=0
    g70: LineSegment StartX=11.2245 StartY=-4.09431 StartZ=0 EndX=11.6861 EndY=-3.91007 EndZ=0
    g71: LineSegment StartX=11.6861 StartY=-3.91007 StartZ=0 EndX=12.1039 EndY=-3.88396 EndZ=0
    g72: LineSegment StartX=12.1039 StartY=-3.88396 StartZ=0 EndX=12.6 EndY=-3.9623 EndZ=0
    g73: LineSegment StartX=12.6 StartY=-3.9623 StartZ=0 EndX=13.5793 EndY=-3.87743 EndZ=0
    g74: LineSegment StartX=13.5793 StartY=-3.87743 StartZ=0 EndX=14.3888 EndY=-3.74687 EndZ=0
    g75: LineSegment StartX=14.3888 StartY=-3.74687 StartZ=0 EndX=14.7544 EndY=-3.68158 EndZ=0
    g76: LineSegment StartX=14.7544 StartY=-3.68158 StartZ=0 EndX=15.2767 EndY=-3.75339 EndZ=0
    g77: LineSegment StartX=15.2767 StartY=-3.75339 StartZ=0 EndX=15.0432 EndY=-3.24137 EndZ=0
    g78: LineSegment StartX=15.0432 StartY=-3.24137 StartZ=0 EndX=14.5209 EndY=-2.51672 EndZ=0
    g79: LineSegment StartX=14.5209 StartY=-2.51672 StartZ=0 EndX=14.0378 EndY=-1.99445 EndZ=0
    g80: LineSegment StartX=14.0378 StartY=-1.99445 StartZ=0 EndX=13.2802 EndY=-1.54625 EndZ=0
    g81: LineSegment StartX=13.2802 StartY=-1.54625 StartZ=0 EndX=13.0438 EndY=-1.23117 EndZ=0
    g82: LineSegment StartX=13.0438 StartY=-1.23117 StartZ=0 EndX=12.1074 EndY=-0.797939 EndZ=0
    g83: LineSegment StartX=12.1074 StartY=-0.797939 StartZ=0 EndX=11.3804 EndY=-0.250878 EndZ=0
    g84: LineSegment StartX=11.3804 StartY=-0.250878 StartZ=0 EndX=10.4396 EndY=0.304889 EndZ=0
    g85: LineSegment StartX=10.4396 StartY=0.304889 StartZ=0 EndX=9.59526 EndY=0.727998 EndZ=0
    g86: LineSegment StartX=9.59526 StartY=0.727998 StartZ=0 EndX=8.53624 EndY=0.97306 EndZ=0
    g87: LineSegment StartX=8.53624 StartY=0.97306 StartZ=0 EndX=7.199 EndY=0.97306 EndZ=0
    g88: LineSegment StartX=7.199 StartY=0.97306 StartZ=0 EndX=5.77932 EndY=0.795578 EndZ=0
    g89: LineSegment StartX=5.77932 StartY=0.795578 StartZ=0 EndX=5.60186 EndY=0.795578 EndZ=0
    g90: LineSegment StartX=5.60186 StartY=0.795578 StartZ=0 EndX=5.83178 EndY=0.981815 EndZ=0
    g91: LineSegment StartX=5.83178 StartY=0.981815 StartZ=0 EndX=6.25403 EndY=1.1582 EndZ=0
    g92: LineSegment StartX=6.30214 StartY=1.38269 StartZ=0 EndX=7.17987 EndY=1.70686 EndZ=0
    g93: LineSegment StartX=7.17987 StartY=1.70686 StartZ=0 EndX=7.44682 EndY=1.79438 EndZ=0
    g94: LineSegment StartX=7.44682 StartY=1.79438 StartZ=0 EndX=7.49058 EndY=2.12696 EndZ=0
    g95: LineSegment StartX=7.49058 StartY=2.12696 StartZ=0 EndX=8.30058 EndY=2.66839 EndZ=0
    g96: LineSegment StartX=8.30058 StartY=2.66839 StartZ=0 EndX=8.68575 EndY=2.81854 EndZ=0
    g97: LineSegment StartX=8.68575 StartY=2.81854 StartZ=0 EndX=8.68575 EndY=3.12537 EndZ=0
    g98: LineSegment StartX=8.68575 StartY=3.12537 StartZ=0 EndX=8.89508 EndY=3.18684 EndZ=0
    g99: LineSegment StartX=8.89508 StartY=3.18684 StartZ=0 EndX=9.63492 EndY=4.06602 EndZ=0
    g100: LineSegment StartX=9.63492 StartY=4.06602 StartZ=0 EndX=9.62638 EndY=4.32743 EndZ=0
    g101: LineSegment StartX=9.62638 StartY=4.32743 StartZ=0 EndX=10.2068 EndY=5.18314 EndZ=0
    g102: LineSegment StartX=10.2068 StartY=5.18314 StartZ=0 EndX=9.25518 EndY=5.64445 EndZ=0
    g103: LineSegment StartX=9.1102 StartY=5.87597 StartZ=0 EndX=8.32132 EndY=5.97336 EndZ=0
    g104: LineSegment StartX=8.32132 StartY=5.97336 StartZ=0 EndX=8.15466 EndY=6.06625 EndZ=0
    g105: LineSegment StartX=7.63471 StartY=6.13088 StartZ=0 EndX=7.56391 EndY=6.33267 EndZ=0
    g106: LineSegment StartX=7.56391 StartY=6.33267 StartZ=0 EndX=6.74832 EndY=6.35496 EndZ=0
    g107: LineSegment StartX=6.74832 StartY=6.35496 StartZ=0 EndX=6.46819 EndY=6.29526 EndZ=0
    g108: LineSegment StartX=6.46819 StartY=6.29526 StartZ=0 EndX=6.27042 EndY=6.61061 EndZ=0
    g109: LineSegment StartX=6.27042 StartY=6.61061 StartZ=0 EndX=5.40453 EndY=6.33267 EndZ=0
    g110: LineSegment StartX=5.40453 StartY=6.33267 StartZ=0 EndX=5.27091 EndY=6.47164 EndZ=0
    g111: LineSegment StartX=5.27091 StartY=6.47164 StartZ=0 EndX=4.56942 EndY=6.24725 EndZ=0
    g112: LineSegment StartX=4.56942 StartY=6.24725 StartZ=0 EndX=4.44161 EndY=6.40652 EndZ=0
    g113: LineSegment StartX=4.44161 StartY=6.40652 StartZ=0 EndX=3.4195 EndY=5.94588 EndZ=0
    g114: LineSegment StartX=3.4195 StartY=5.94588 StartZ=0 EndX=3.29192 EndY=6.1532 EndZ=0
    g115: LineSegment StartX=3.29192 StartY=6.1532 StartZ=0 EndX=2.15964 EndY=5.49137 EndZ=0
    g116: LineSegment StartX=2.15964 StartY=5.49137 StartZ=0 EndX=2.00016 EndY=5.69869 EndZ=0
    g117: LineSegment StartX=2.00016 StartY=5.69869 StartZ=0 EndX=1.6185 EndY=5.34828 EndZ=0
    g118: LineSegment StartX=1.6185 StartY=5.34828 StartZ=0 EndX=1.45984 EndY=5.94974 EndZ=0
    g119: LineSegment StartX=1.38165 StartY=6.28651 StartZ=0 EndX=1.14534 EndY=6.29963 EndZ=0
    g120: LineSegment StartX=0.348522 StartY=7.29544 StartZ=0 EndX=0.126706 EndY=7.68126 EndZ=0
    g121: LineSegment StartX=0.126706 StartY=7.68126 StartZ=0 EndX=-0.415308 EndY=8.18163 EndZ=0
    g122: LineSegment StartX=-0.415308 StartY=8.18163 StartZ=0 EndX=-0.872658 EndY=8.6237 EndZ=0
    g123: LineSegment StartX=-0.872658 StartY=8.6237 StartZ=0 EndX=-1.12074 EndY=8.64329 EndZ=0
    g124: LineSegment StartX=-1.12074 StartY=8.64329 StartZ=0 EndX=-1.79316 EndY=9.11986 EndZ=0
    g125: LineSegment StartX=-1.79316 StartY=9.11986 StartZ=0 EndX=-2.31488 EndY=9.12122 EndZ=0
    g126: LineSegment StartX=-2.31488 StartY=9.12122 StartZ=0 EndX=-2.71321 EndY=9.13846 EndZ=0
    g127: LineSegment StartX=-2.71321 StartY=9.13846 StartZ=0 EndX=-2.88425 EndY=9.34157 EndZ=0
    g128: LineSegment StartX=-2.88425 StartY=9.34157 StartZ=0 EndX=-3.16779 EndY=9.26454 EndZ=0
    g129: LineSegment StartX=-3.70739 StartY=9.82796 StartZ=0 EndX=-4.04915 EndY=9.7003 EndZ=0
    g130: LineSegment StartX=-4.04915 StartY=9.7003 StartZ=0 EndX=-4.42988 EndY=10.011 EndZ=0
    g131: LineSegment StartX=-5.98947 StartY=10.3656 StartZ=0 EndX=-7.32605 EndY=10.4108 EndZ=0
    g132: LineSegment StartX=-7.25254 StartY=9.13254 StartZ=0 EndX=-7.36878 EndY=8.7693 EndZ=0
    g133: LineSegment StartX=-7.36878 StartY=8.7693 StartZ=0 EndX=-7.2614 EndY=7.83762 EndZ=0
    g134: LineSegment StartX=-7.2614 StartY=7.83762 StartZ=0 EndX=-7.41112 EndY=7.6042 EndZ=0
    g135: LineSegment StartX=-7.41112 StartY=7.6042 StartZ=0 EndX=-7.09216 EndY=6.74302 EndZ=0
    g136: LineSegment StartX=-7.09216 StartY=6.74302 StartZ=0 EndX=-7.10014 EndY=6.55962 EndZ=0
    g137: LineSegment StartX=-7.10014 StartY=6.55962 StartZ=0 EndX=-7.29151 EndY=6.3842 EndZ=0
    g138: LineSegment StartX=-7.29151 StartY=6.3842 StartZ=0 EndX=-6.74132 EndY=5.29976 EndZ=0
    g139: LineSegment StartX=-6.74132 StartY=5.29976 StartZ=0 EndX=-6.87495 EndY=5.02732 EndZ=0
    g140: LineSegment StartX=-6.87495 StartY=5.02732 StartZ=0 EndX=-6.31586 EndY=4.42065 EndZ=0
    g141: LineSegment StartX=-6.31586 StartY=4.42065 StartZ=0 EndX=-6.30396 EndY=4.19463 EndZ=0
    g142: LineSegment StartX=-6.30396 StartY=4.19463 StartZ=0 EndX=-6.05415 EndY=4.0043 EndZ=0
    g143: LineSegment StartX=-6.05415 StartY=4.0043 StartZ=0 EndX=-6.18501 EndY=3.95672 EndZ=0
    g144: LineSegment StartX=-6.18501 StartY=3.95672 StartZ=0 EndX=-5.54265 EndY=3.07645 EndZ=0
    g145: LineSegment StartX=-5.54265 StartY=3.07645 StartZ=0 EndX=-5.57833 EndY=2.90991 EndZ=0
    g146: LineSegment StartX=-5.57833 StartY=2.90991 StartZ=0 EndX=-5.1263 EndY=2.41029 EndZ=0
    g147: LineSegment StartX=-5.1263 StartY=2.41029 StartZ=0 EndX=-5.18578 EndY=2.26755 EndZ=0
    g148: LineSegment StartX=-5.18578 StartY=2.26755 StartZ=0 EndX=-4.73375 EndY=1.89878 EndZ=0
    g149: LineSegment StartX=-4.73375 StartY=1.89878 StartZ=0 EndX=-4.42446 EndY=1.5895 EndZ=0
    g150: LineSegment StartX=-4.42446 StartY=1.5895 StartZ=0 EndX=-5.31663 EndY=1.29211 EndZ=0
    g151: LineSegment StartX=-5.31663 StartY=1.29211 StartZ=0 EndX=-5.84004 EndY=1.08988 EndZ=0
    g152: LineSegment StartX=-5.84004 StartY=1.08988 StartZ=0 EndX=-6.04226 EndY=0.792495 EndZ=0
    g153: LineSegment StartX=-6.04226 StartY=0.792495 StartZ=0 EndX=-6.94632 EndY=0.994719 EndZ=0
    g154: LineSegment StartX=-6.94632 StartY=0.994719 StartZ=0 EndX=-7.19613 EndY=0.887659 EndZ=0
    g155: LineSegment StartX=-7.19613 StartY=0.887659 StartZ=0 EndX=-7.8147 EndY=1.0423 EndZ=0
    g156: LineSegment StartX=-7.8147 StartY=1.0423 StartZ=0 EndX=-8.02502 EndY=0.969153 EndZ=0
    g157: LineSegment StartX=-8.02502 StartY=0.969153 StartZ=0 EndX=-8.60267 EndY=1.03042 EndZ=0
    g158: LineSegment StartX=-8.60267 StartY=1.03042 StartZ=0 EndX=-8.8346 EndY=0.872878 EndZ=0
    g159: LineSegment StartX=-8.8346 StartY=0.872878 StartZ=0 EndX=-9.33349 EndY=0.929767 EndZ=0
    g160: LineSegment StartX=-9.33349 StartY=0.929767 StartZ=0 EndX=-9.66169 EndY=0.649695 EndZ=0
    g161: LineSegment StartX=-9.66169 StartY=0.649695 StartZ=0 EndX=-10.3249 EndY=0.649695 EndZ=0
    g162: LineSegment StartX=-10.3249 StartY=0.649695 StartZ=0 EndX=-11.0107 EndY=0.32425 EndZ=0
    g163: LineSegment StartX=-11.0107 StartY=0.32425 StartZ=0 EndX=-11.7283 EndY=0.053139 EndZ=0
    g164: LineSegment StartX=-11.7283 StartY=0.053139 StartZ=0 EndX=-12.2971 EndY=-0.13161 EndZ=0
    g165: LineSegment StartX=-12.2971 StartY=-0.13161 StartZ=0 EndX=-12.4212 EndY=-0.347049 EndZ=0
    g166: LineSegment StartX=-12.4212 StartY=-0.347049 StartZ=0 EndX=-13.296 EndY=-0.817096 EndZ=0
    g167: LineSegment StartX=-13.296 StartY=-0.817096 StartZ=0 EndX=-13.9227 EndY=-1.24144 EndZ=0
    g168: LineSegment StartX=-13.9227 StartY=-1.24144 StartZ=0 EndX=-14.1708 EndY=-1.59398 EndZ=0
    g169: LineSegment StartX=-14.1708 StartY=-1.59398 StartZ=0 EndX=-14.5386 EndY=-2.09216 EndZ=0
    g170: LineSegment StartX=-14.5386 StartY=-2.09216 StartZ=0 EndX=-14.7831 EndY=-2.4577 EndZ=0
    g171: LineSegment StartX=-14.7831 StartY=-2.4577 StartZ=0 EndX=-15.0667 EndY=-2.9879 EndZ=0
    g172: LineSegment StartX=7.82861 StartY=6.04487 StartZ=0 EndX=7.63471 EndY=6.13088 EndZ=0
    g173: LineSegment StartX=-14.4175 StartY=-3.20194 StartZ=0 EndX=-14.1386 EndY=-3.3581 EndZ=0
    g174: LineSegment StartX=-13.8673 StartY=-3.55064 StartZ=0 EndX=-13.4107 EndY=-3.57136 EndZ=0
    g175: LineSegment StartX=-13.1321 StartY=-3.61699 StartZ=0 EndX=-12.817 EndY=-3.62343 EndZ=0
    g176: LineSegment StartX=-12.817 StartY=-3.62343 StartZ=0 EndX=-12.4662 EndY=-3.85302 EndZ=0
    g177: LineSegment StartX=-13.4107 StartY=-3.57136 StartZ=0 EndX=-13.1321 EndY=-3.61699 EndZ=0
    g178: LineSegment StartX=-12.4662 StartY=-3.85302 StartZ=0 EndX=-11.8704 EndY=-3.85302 EndZ=0
    g179: LineSegment StartX=-11.8704 StartY=-3.85302 StartZ=0 EndX=-11.5204 EndY=-4.00836 EndZ=0
    g180: LineSegment StartX=-11.5204 StartY=-4.00836 StartZ=0 EndX=-11.1389 EndY=-4.05555 EndZ=0
    g181: LineSegment StartX=-11.1389 StartY=-4.05555 StartZ=0 EndX=-10.8098 EndY=-4.00788 EndZ=0
    g182: LineSegment StartX=-9.89036 StartY=-4.3898 StartZ=0 EndX=-9.99555 EndY=-4.87697 EndZ=0
    g183: LineSegment StartX=-9.99555 StartY=-4.87697 StartZ=0 EndX=-10.0894 EndY=-5.36391 EndZ=0
    g184: LineSegment StartX=-10.0894 StartY=-5.36391 StartZ=0 EndX=-10.107 EndY=-5.50471 EndZ=0
    g185: LineSegment StartX=-10.107 StartY=-5.50471 StartZ=0 EndX=-9.77848 EndY=-5.63965 EndZ=0
    g186: LineSegment StartX=-9.77848 StartY=-5.63965 StartZ=0 EndX=-9.51656 EndY=-5.73022 EndZ=0
    g187: LineSegment StartX=-4.19735 StartY=-5.16248 StartZ=0 EndX=-3.75191 EndY=-4.97251 EndZ=0
    g188: LineSegment StartX=-2.38042 StartY=-4.51801 StartZ=0 EndX=-2.15112 EndY=-4.35765 EndZ=0
    g189: LineSegment StartX=-3.4685 StartY=-8.65617 StartZ=0 EndX=-3.27268 EndY=-8.56671 EndZ=0
    g190: LineSegment StartX=-3.16823 StartY=-8.76909 StartZ=0 EndX=-3.07088 EndY=-9.32083 EndZ=0
    g191: LineSegment StartX=2.58839 StartY=-7.69871 StartZ=0 EndX=2.6542 EndY=-7.03945 EndZ=0
    g192: LineSegment StartX=8.0902 StartY=-3.99438 StartZ=0 EndX=8.4103 EndY=-4.11103 EndZ=0
    g193: LineSegment StartX=9.82964 StartY=-4.15887 StartZ=0 EndX=10.1326 EndY=-3.9675 EndZ=0
    g194: LineSegment StartX=6.30214 StartY=1.38269 StartZ=0 EndX=6.25403 EndY=1.1582 EndZ=0
    g195: LineSegment StartX=1.38165 StartY=6.28651 StartZ=0 EndX=1.45984 EndY=5.94974 EndZ=0
    g196: LineSegment StartX=0.348522 StartY=7.29544 StartZ=0 EndX=0.824344 EndY=6.91479 EndZ=0
    g197: LineSegment StartX=0.824344 StartY=6.91479 StartZ=0 EndX=1.14534 EndY=6.29963 EndZ=0
    g198: LineSegment StartX=-3.70739 StartY=9.82796 StartZ=0 EndX=-3.16779 EndY=9.26454 EndZ=0
    g199: LineSegment StartX=-5.98947 StartY=10.3656 StartZ=0 EndX=-5.43038 EndY=10.4489 EndZ=0
    g200: LineSegment StartX=-5.43038 StartY=10.4489 StartZ=0 EndX=-4.9791 EndY=10.1425 EndZ=0
    g201: LineSegment StartX=-4.42988 StartY=10.011 StartZ=0 EndX=-4.9791 EndY=10.1425 EndZ=0
    g202: LineSegment StartX=-7.25254 StartY=9.13254 StartZ=0 EndX=-7.32605 EndY=10.4108 EndZ=0
    g203: LineSegment StartX=7.82861 StartY=6.04487 StartZ=0 EndX=8.15466 EndY=6.06625 EndZ=0
    g204: LineSegment StartX=9.1102 StartY=5.87597 StartZ=0 EndX=9.25518 EndY=5.64445 EndZ=0
  constraints (114):
    c: Coincident(g4,g3)
    c: Coincident(g6,g5)
    c: Coincident(g8,g7)
    c: Coincident(g9,g8)
    c: Coincident(g10,g9)
    c: Coincident(g11,g10)
    c: Coincident(g13,g12)
    c: Coincident(g16,g15)
    c: Coincident(g22,g21)
    c: Coincident(g25,g24)
    c: Coincident(g26,g25)
    c: Coincident(g28,g27)
    c: Coincident(g33,g32)
    c: Coincident(g37,g36)
    c: Coincident(g38,g37)
    c: Coincident(g40,g39)
    c: Coincident(g44,g43)
    c: Coincident(g51,g50)
    c: Coincident(g52,g51)
    c: Coincident(g57,g56)
    c: Coincident(g58,g57)
    c: Coincident(g59,g58)
    c: Coincident(g61,g60)
    c: Coincident(g63,g62)
    c: Coincident(g66,g65)
    c: Coincident(g70,g69)
    c: Coincident(g72,g71)
    c: Coincident(g73,g72)
    c: Coincident(g74,g73)
    c: Coincident(g77,g76)
    c: Coincident(g80,g79)
    c: Coincident(g81,g80)
    c: Coincident(g83,g82)
    c: Coincident(g85,g84)
    c: Coincident(g86,g85)
    c: Coincident(g87,g86)
    c: Coincident(g89,g88)
    c: Coincident(g90,g89)
    c: Coincident(g91,g90)
    c: Coincident(g93,g92)
    c: Coincident(g95,g94)
    c: Coincident(g97,g96)
    c: Coincident(g98,g97)
    c: Coincident(g99,g98)
    c: Coincident(g100,g99)
    c: Coincident(g104,g103)
    c: Coincident(g106,g105)
    c: Coincident(g107,g106)
    c: Coincident(g111,g110)
    c: Coincident(g113,g112)
    c: Coincident(g118,g117)
    c: Coincident(g122,g121)
    c: Coincident(g126,g125)
    c: Coincident(g130,g129)
    c: Coincident(g133,g132)
    c: Coincident(g134,g133)
    c: Coincident(g135,g134)
    c: Coincident(g139,g138)
    c: Coincident(g142,g141)
    c: Coincident(g156,g155)
    c: Coincident(g157,g156)
    c: Coincident(g159,g158)
    c: Coincident(g161,g160)
    c: Coincident(g164,g163)
    c: Coincident(g165,g164)
    c: Coincident(g168,g167)
    c: Coincident(g169,g168)
    c: Coincident(g171,g170)
    c: Coincident(g171,g0)
    c: Coincident(g172,g105)
    c: DistanceX(g165) = -12.4212
    c: DistanceY(g165) = -0.347049
    c: Coincident(g173,g0)
    c: Coincident(g173,g1)
    c: Coincident(g174,g1)
    c: Coincident(g177,g174)
    c: Coincident(g177,g175)
    c: Coincident(g178,g176)
    c: Coincident(g181,g2)
    c: Coincident(g182,g4)
    c: Coincident(g186,g185)
    c: Coincident(g186,g5)
    c: Coincident(g187,g16)
    c: Coincident(g187,g17)
    c: Coincident(g188,g21)
    c: Coincident(g188,g20)
    c: Coincident(g189,g28)
    c: Coincident(g189,g29)
    c: Coincident(g190,g29)
    c: Coincident(g190,g30)
    c: Coincident(g191,g42)
    c: Coincident(g191,g43)
    c: Coincident(g192,g63)
    c: Coincident(g192,g64)
    c: Coincident(g193,g66)
    c: Coincident(g193,g67)
    c: Coincident(g194,g92)
    c: Coincident(g194,g91)
    c: Coincident(g195,g119)
    c: Coincident(g195,g118)
    c: Coincident(g196,g120)
    c: Coincident(g197,g119)
    c: Coincident(g198,g129)
    c: Coincident(g198,g128)
    c: Coincident(g199,g131)
    c: Coincident(g200,g199)
    c: Coincident(g201,g130)
    c: Coincident(g201,g200)
    c: Coincident(g202,g132)
    c: Coincident(g202,g131)
    c: Coincident(g203,g172)
    c: Coincident(g203,g104)
    c: Coincident(g204,g103)
    c: Coincident(g204,g102)
FEATURE [PartDesign::Pad] Pad002
  Direction = (0,0,1)
  Length = 3
  Length2 = 10
  Profile = -> Sketch002
  ReferenceAxis = -> Sketch002 [N_Axis]
  Type = 0
FEATURE [PartDesign::Body] Body002  label="logo004"
  Group = -> [Sketch002,Pad002]
  Origin = -> Origin002
  Placement = pos=(39.35,-43,30) rot=(1,0,0;1.5708rad)
  Tip = -> Pad002
FEATURE [Part::MultiFuse] Fusion041  label="logo005"
  Placement = pos=(-69,-26,58) rot=(1,0,0;3.14159rad)
  Shapes = -> [Body002,Box069]
